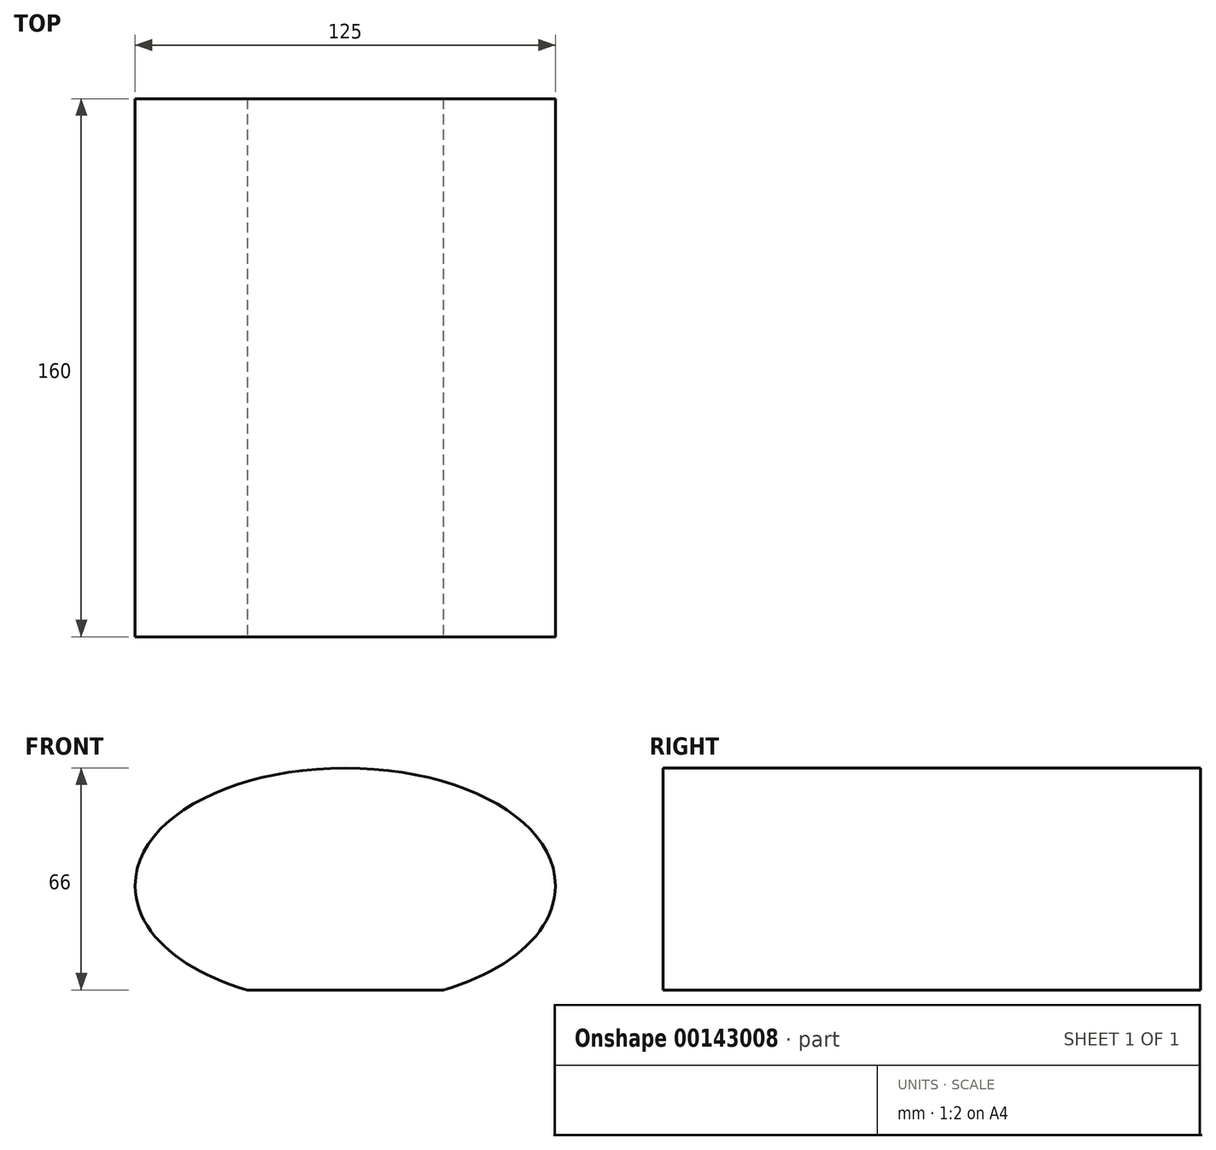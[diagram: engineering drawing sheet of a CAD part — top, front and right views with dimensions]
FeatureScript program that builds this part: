
annotation { "Feature Type Name" : "Feature", "Feature Type Description" : "" }
export const myFeature = defineFeature(function(context is Context, id is Id, definition is map)
    precondition{}
    {
        {
            var Q0;
            Q0=qCreatedBy(makeId("Front.planeOp"),FACE);
            var sketch = newSketch(context, id + "F0", { "sketchPlane" : qUnion([Q0])});
            skLineSegment(sketch, "E0.bottom", {"start": v(0, 0) * mm, "end": v(125, 0) * mm, "construction": true});
            skLineSegment(sketch, "E0.top", {"start": v(0, 70) * mm, "end": v(125, 70) * mm, "construction": true});
            skLineSegment(sketch, "E0.left", {"start": v(0, 0) * mm, "end": v(0, 70) * mm, "construction": true});
            skLineSegment(sketch, "E0.right", {"start": v(125, 0) * mm, "end": v(125, 70) * mm, "construction": true});
            skLineSegment(sketch, "E1", {"start": v(62.5, 70) * mm, "end": v(62.5, 0) * mm, "construction": true});
            skPoint(sketch, "E1.startSnap0", {"position": v(62.5, 70) * mm});
            skPoint(sketch, "E1.endSnap0", {"position": v(62.5, 0) * mm});
            skLineSegment(sketch, "E2", {"start": v(0, 35) * mm, "end": v(125, 35) * mm, "construction": true});
            skFitSpline(sketch, "E3", {"points": [v(0, 35) * mm, v(62.5, 70) * mm], "startDerivative": vector(0, 60.8) * mm, "endDerivative": vector(100.4, 0) * mm});
            skFitSpline(sketch, "E4.MirrorCS", {"points": [v(125, 35) * mm, v(62.5, 70) * mm], "startDerivative": vector(0, 60.8) * mm, "endDerivative": vector(-100.4, 0) * mm});
            skLineSegment(sketch, "E5", {"start": v(32.9, 0) * mm, "end": v(92.1, 0) * mm, "construction": true});
            skFitSpline(sketch, "E6.MirrorCS", {"points": [v(0, 35) * mm, v(62.5, 0) * mm], "startDerivative": vector(0, -60.8) * mm, "endDerivative": vector(100.4, 0) * mm});
            skFitSpline(sketch, "E7.MirrorCS", {"points": [v(125, 35) * mm, v(62.5, 0) * mm], "startDerivative": vector(0, -60.8) * mm, "endDerivative": vector(-100.4, 0) * mm});
            skPoint(sketch, "E8", {"position": v(62.5, 4) * mm});
            skLineSegment(sketch, "E9", {"start": v(62.5, 4) * mm, "end": v(91.7, 4) * mm});
            skLineSegment(sketch, "E10", {"start": v(62.5, 4) * mm, "end": v(33.3, 4) * mm});
            skSolve(sketch);
        }
        {
            var Q0;
            {var subQ4=sQuery(id+"F0.wireOp",EDGE,"E3");Q0=makeQuery(id+"F0.imprint","IMPRINT",FACE,{"disambiguationData":[TD([[makeQuery(id+"F0.imprint","IMPRINT",EDGE,{"derivedFrom":subQ4}),-1.0]])]});}
            extrude(context, id + "F1", {"entities" : qUnion([Q0]), "oppositeDirection" : true, "depth" : 160 * mm});
        }
    });
